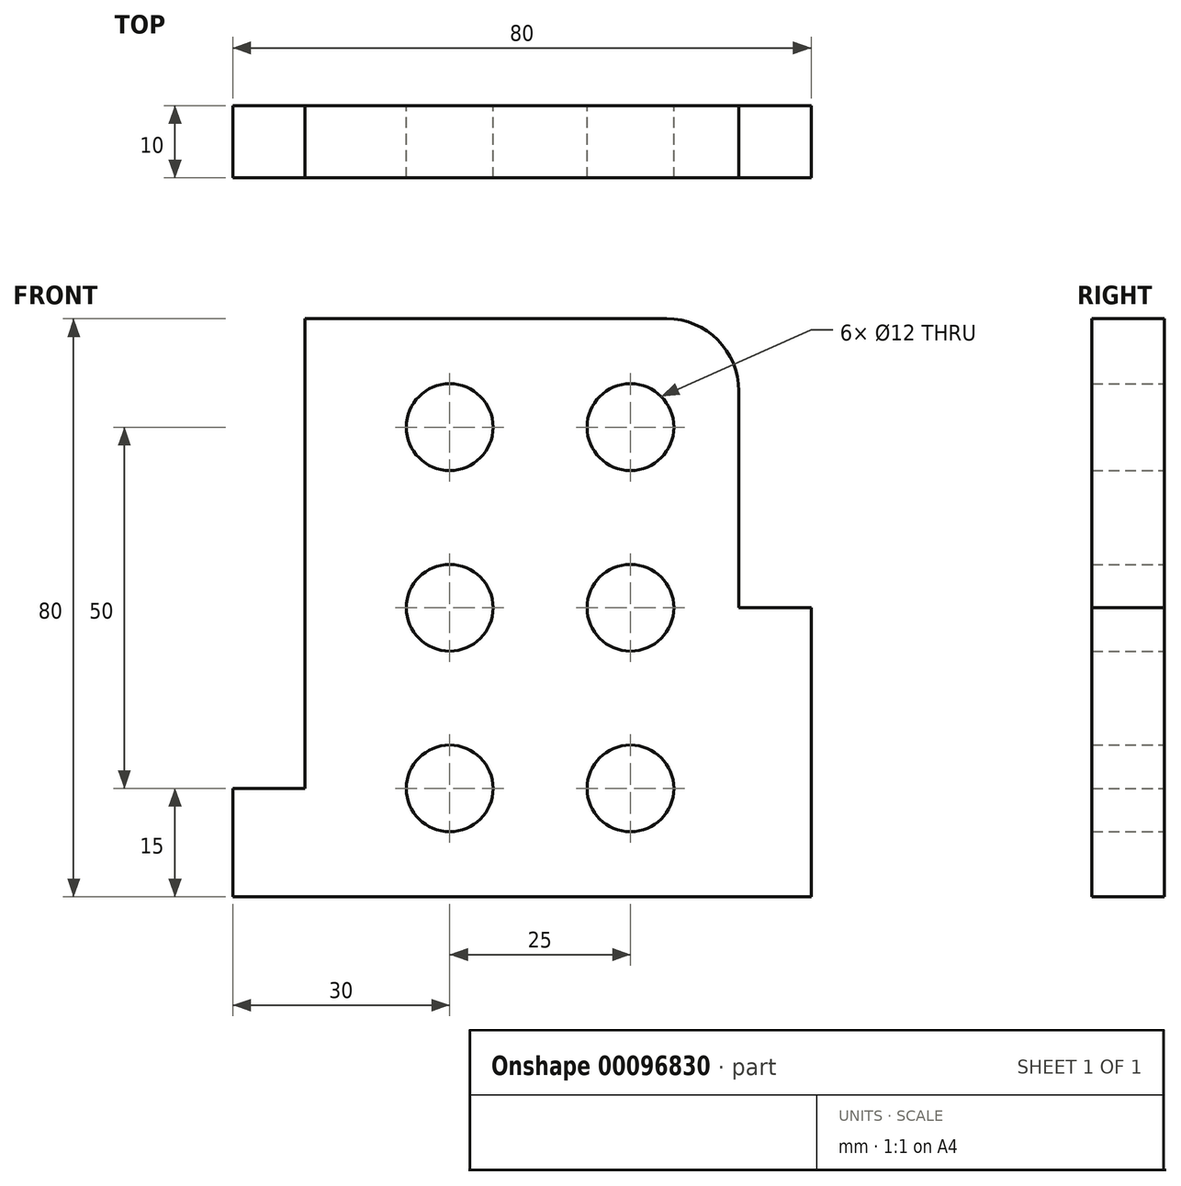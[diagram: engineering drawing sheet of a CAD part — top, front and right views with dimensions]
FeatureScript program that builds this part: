
annotation { "Feature Type Name" : "Feature", "Feature Type Description" : "" }
export const myFeature = defineFeature(function(context is Context, id is Id, definition is map)
    precondition{}
    {
        {
            var Q0;
            Q0=qCreatedBy(makeId("Front.planeOp"),FACE);
            var sketch = newSketch(context, id + "F0", { "sketchPlane" : qUnion([Q0])});
            skLineSegment(sketch, "E0", {"start": v(0, 0) * mm, "end": v(80, 0) * mm});
            skLineSegment(sketch, "E1", {"start": v(80, 0) * mm, "end": v(80, 40) * mm});
            skLineSegment(sketch, "E2", {"start": v(80, 40) * mm, "end": v(70, 40) * mm});
            skLineSegment(sketch, "E3", {"start": v(0, 0) * mm, "end": v(0, 15) * mm});
            skLineSegment(sketch, "E4", {"start": v(0, 15) * mm, "end": v(10, 15) * mm});
            skLineSegment(sketch, "E5", {"start": v(10, 15) * mm, "end": v(10, 80) * mm});
            skLineSegment(sketch, "E6", {"start": v(10, 80) * mm, "end": v(60, 80) * mm});
            skArc(sketch, "E7", {"start": v(60, 80) * mm, "mid": v(67.07, 77.07) * mm, "end": v(70, 70) * mm});
            skLineSegment(sketch, "E8", {"start": v(70, 40) * mm, "end": v(70, 70) * mm});
            skCircle(sketch, "E9", {"center": v(30, 15) * mm, "radius": 6 * mm});
            skCircle(sketch, "E10", {"center": v(55, 15) * mm, "radius": 6 * mm});
            skCircle(sketch, "E11", {"center": v(55, 40) * mm, "radius": 6 * mm});
            skCircle(sketch, "E12", {"center": v(30, 40) * mm, "radius": 6 * mm});
            skCircle(sketch, "E13", {"center": v(55, 65) * mm, "radius": 6 * mm});
            skCircle(sketch, "E14", {"center": v(30, 65) * mm, "radius": 6 * mm});
            skSolve(sketch);
        }
        {
            var Q0;
            Q0 = qSketchRegion(id + "F0", true);
            extrude(context, id + "F1", {"entities" : qUnion([Q0]), "depth" : 10 * mm});
        }
    });
